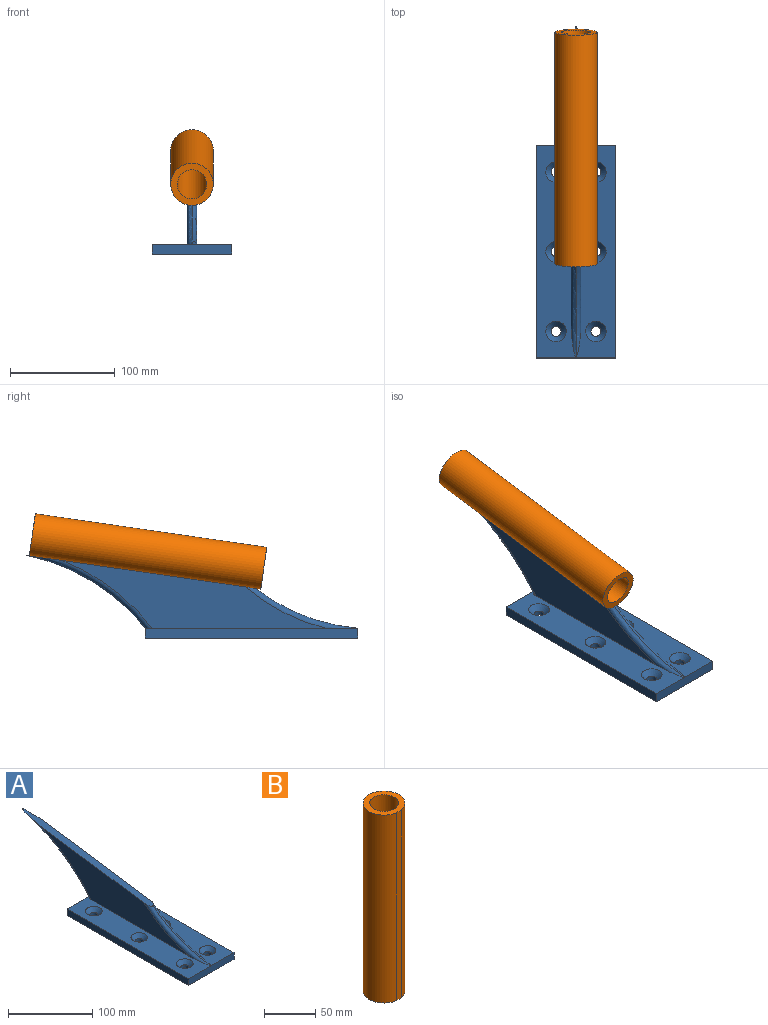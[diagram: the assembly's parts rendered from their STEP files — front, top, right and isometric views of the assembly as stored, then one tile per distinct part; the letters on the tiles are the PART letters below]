
ASSEMBLY  parts=2 mates=1
PART A: 25 faces, bbox 76.2x317.3x119.4 mm
  f0: plane 203.2x76.2mm, normal (0,0,1), area 11828mm2, adj f3,f4,f5,f6,f7,f8,f15,f16
  f1: plane 203.2x76.2mm, normal (0,0,-1), area 15056.3mm2, adj f5,f6,f7,f8,f9,f10,f11,f12
  f2: plane 219.32x31.73mm, normal (0,-0.14,0.99), area 1985.2mm2, adj f3,f4,f21,f22,f23,f24
  f3: plane 251.84x64.88mm, normal (1,0,0), area 7046.5mm2, adj f0,f2,f21,f23
  f4: plane 251.84x64.88mm, normal (-1,0,0), area 7046.5mm2, adj f0,f2,f22,f24
  f5: plane 76.2x9.53mm, normal (0,-1,0), area 725.8mm2, adj f0,f1,f6,f8
  f6: plane 203.2x9.53mm, normal (-1,0,0), area 1935.5mm2, adj f0,f1,f5,f7
  f7: plane 76.2x9.53mm, normal (0,1,0), area 725.8mm2, adj f0,f1,f6,f8
  f8: plane 203.2x9.53mm, normal (1,0,0), area 1935.5mm2, adj f0,f1,f5,f7
  f9: cylinder r=4.76mm len=9.53mm, axis (0,0,-1), area 133mm2, adj f1,f15
  f10: cylinder r=4.76mm len=9.53mm, axis (0,0,-1), area 133mm2, adj f1,f16
  f11: cylinder r=4.76mm len=9.53mm, axis (0,0,-1), area 133mm2, adj f1,f17
  f12: cylinder r=4.76mm len=9.53mm, axis (0,0,-1), area 133mm2, adj f1,f19
  f13: cylinder r=4.76mm len=9.53mm, axis (0,0,-1), area 133mm2, adj f1,f18
  f14: cylinder r=4.76mm len=9.53mm, axis (0,0,-1), area 133mm2, adj f1,f20
  f15: cone r=9.84mm half-angle=45deg, axis (0,0,1), area 329.6mm2, adj f0,f9
  f16: cone r=9.84mm half-angle=45deg, axis (0,0,1), area 329.6mm2, adj f0,f10
  f17: cone r=9.84mm half-angle=45deg, axis (0,0,1), area 329.6mm2, adj f0,f11
  f18: cone r=4.76mm half-angle=45deg, axis (0,0,1), area 329.6mm2, adj f0,f13
  f19: cone r=4.76mm half-angle=45deg, axis (0,0,1), area 329.6mm2, adj f0,f12
  f20: cone r=4.76mm half-angle=45deg, axis (0,0,1), area 329.6mm2, adj f0,f14
  f21: torus R=203.52mm, axis (1,0,0), area 944.3mm2, adj f0,f2,f3,f22
  f22: torus R=203.52mm, axis (1,0,0), area 944.3mm2, adj f0,f2,f4,f21
  f23: torus R=188.24mm, axis (1,0,0), area 741.5mm2, adj f0,f2,f3,f24
  f24: torus R=188.24mm, axis (1,0,0), area 741.5mm2, adj f0,f2,f4,f23
PART B: 5 faces, bbox 40.6x40.5x223.5 mm
  f0: cylinder r=20.32mm len=223.52mm, axis (0,0,-1), area 27112.6mm2, adj f2,f3,f4
  f1: cylinder r=13.97mm len=223.52mm, axis (0,0,-1), area 19619.7mm2, adj f3,f4
  f2: plane 223.52x6.35mm, normal (0.03,-1,0), area 1419.4mm2, adj f0,f3,f4
  f3: plane 40.64x40.47mm, normal (0,0,1), area 683mm2, adj f0,f1,f2
  f4: plane 40.64x40.47mm, normal (0,0,-1), area 683mm2, adj f0,f1,f2
PLACE A t=(-68.35,-52.8,45.65)mm
PLACE B rot(axis=(1,0.01,-0.01),98.2deg) t=(-63.59,160.52,134.89)mm
MATE fastened A.f2 <-> B.f2  axis (0,-0.14,0.99) through (-63.59,52.79,99.03)mm
